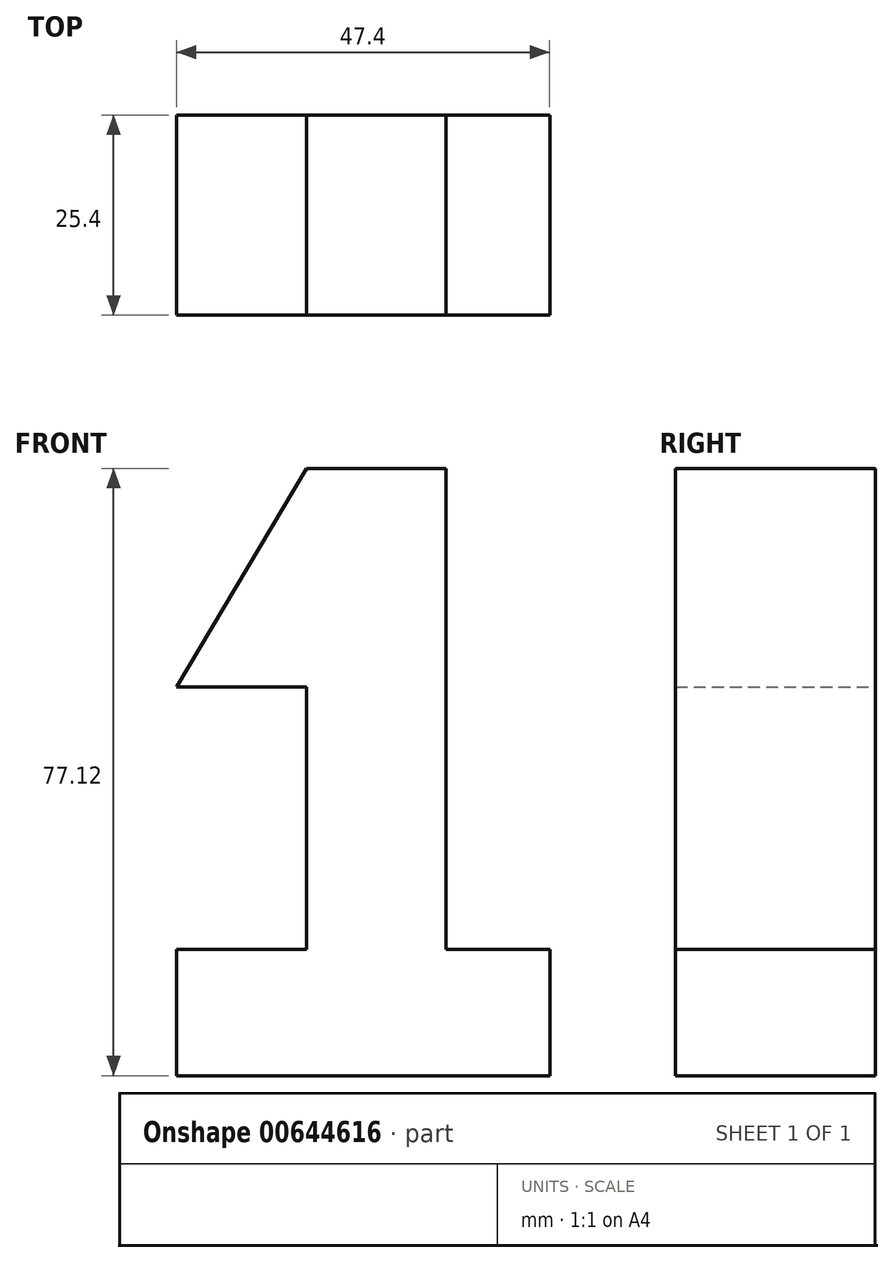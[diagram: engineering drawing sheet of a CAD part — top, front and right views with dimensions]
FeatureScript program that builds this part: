
annotation { "Feature Type Name" : "Feature", "Feature Type Description" : "" }
export const myFeature = defineFeature(function(context is Context, id is Id, definition is map)
    precondition{}
    {
        {
            var Q0;
            Q0=qCreatedBy(makeId("Front.planeOp"),FACE);
            var sketch = newSketch(context, id + "F0", { "sketchPlane" : qUnion([Q0])});
            skLineSegment(sketch, "E0.bottom", {"start": v(0, 77.12) * mm, "end": v(17.7, 77.12) * mm});
            skLineSegment(sketch, "E0.top", {"start": v(0, 0) * mm, "end": v(17.7, 0) * mm});
            skLineSegment(sketch, "E0.left", {"start": v(0, 49.37) * mm, "end": v(0, 16.07) * mm});
            skLineSegment(sketch, "E0.right", {"start": v(17.7, 77.12) * mm, "end": v(17.7, 16.07) * mm});
            skLineSegment(sketch, "E1", {"start": v(0, 77.12) * mm, "end": v(-16.53, 49.37) * mm});
            skLineSegment(sketch, "E2", {"start": v(-16.53, 49.37) * mm, "end": v(0, 49.37) * mm});
            skPoint(sketch, "E3.firstSnap0", {"position": v(8.85, 0) * mm});
            skLineSegment(sketch, "E3.bottom", {"start": v(30.87, 0) * mm, "end": v(-16.53, 0) * mm});
            skLineSegment(sketch, "E3.top", {"start": v(30.87, 16.07) * mm, "end": v(17.7, 16.07) * mm});
            skLineSegment(sketch, "E3.left", {"start": v(30.87, 0) * mm, "end": v(30.87, 16.07) * mm});
            skLineSegment(sketch, "E3.right", {"start": v(-16.53, 0) * mm, "end": v(-16.53, 16.07) * mm});
            skLineSegment(sketch, "E4.trimOffspring", {"start": v(0, 16.07) * mm, "end": v(-16.53, 16.07) * mm});
            skSolve(sketch);
        }
        {
            var Q0;
            Q0 = qSketchRegion(id + "F0", true);
            extrude(context, id + "F1", {"entities" : qUnion([Q0]), "depth" : 25.4 * mm, "offsetDistance" : 25.4 * mm});
        }
    });
